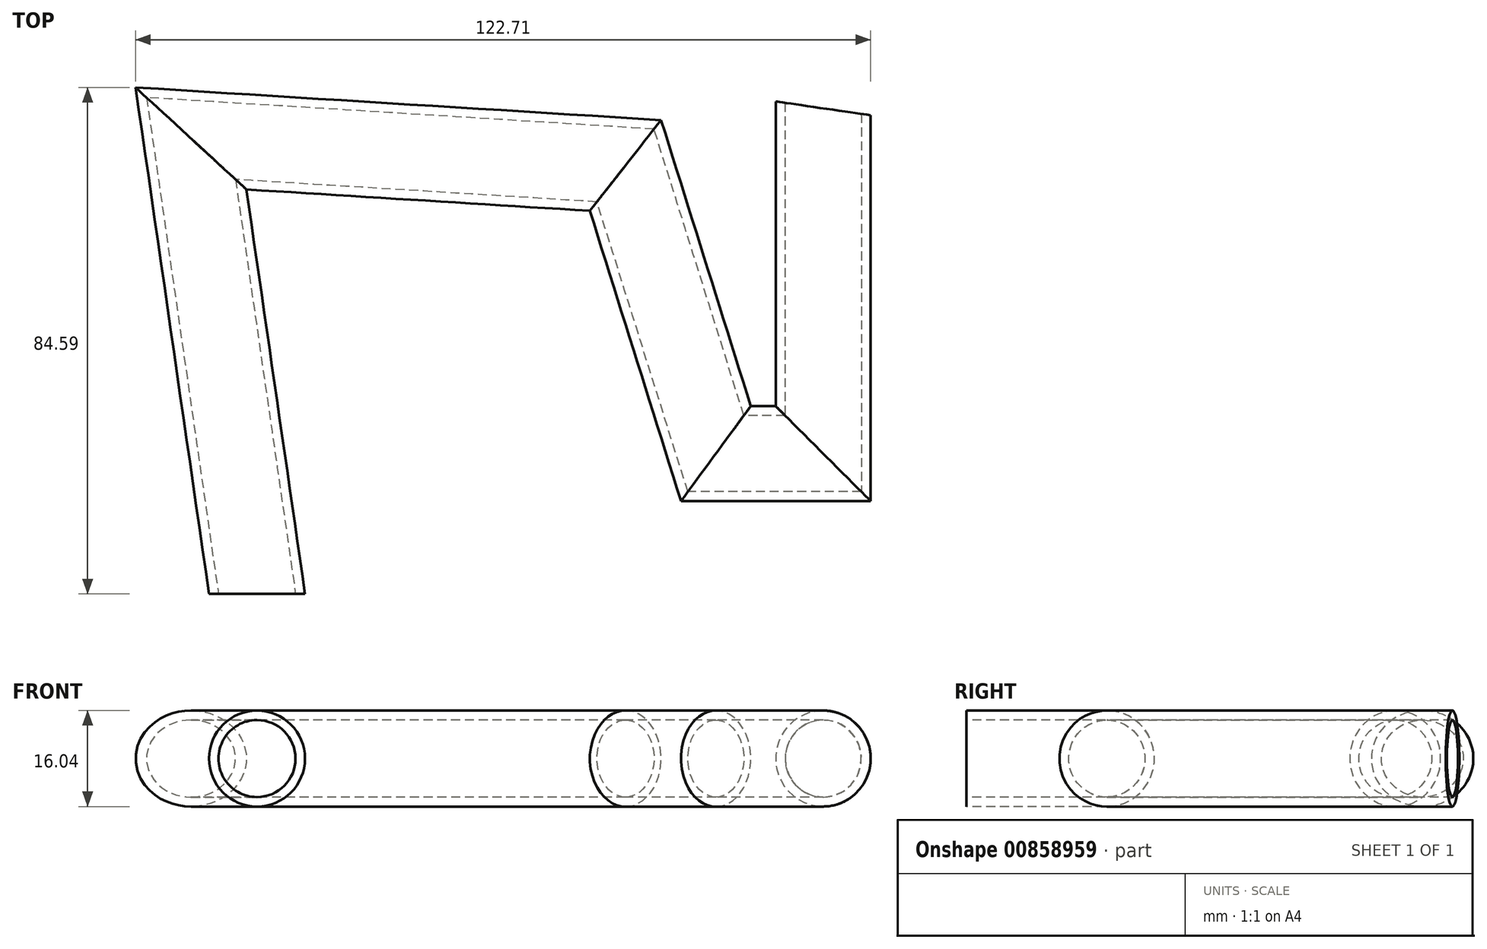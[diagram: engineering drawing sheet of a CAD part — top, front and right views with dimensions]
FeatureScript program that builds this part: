
annotation { "Feature Type Name" : "Feature", "Feature Type Description" : "" }
export const myFeature = defineFeature(function(context is Context, id is Id, definition is map)
    precondition{}
    {
        {
            var Q0;
            Q0=qCreatedBy(makeId("Top.planeOp"),FACE);
            var sketch = newSketch(context, id + "F0", { "sketchPlane" : qUnion([Q0])});
            skLineSegment(sketch, "E0", {"start": v(-37.35, -58.1) * mm, "end": v(-48, 15.52) * mm});
            skLineSegment(sketch, "E1", {"start": v(-48, 15.52) * mm, "end": v(20.13, 11.29) * mm});
            skLineSegment(sketch, "E2", {"start": v(20.13, 11.29) * mm, "end": v(35.25, -36.96) * mm});
            skLineSegment(sketch, "E3", {"start": v(35.25, -36.96) * mm, "end": v(57.14, -36.96) * mm});
            skLineSegment(sketch, "E4", {"start": v(57.14, -36.96) * mm, "end": v(57.14, 22.68) * mm});
            skSolve(sketch);
        }
        {
            var Q0;
            Q0=qCreatedBy(makeId("Front.planeOp"),FACE);
            var sketch = newSketch(context, id + "F1", { "sketchPlane" : qUnion([Q0])});
            skCircle(sketch, "E5", {"center": v(-48.07, 0) * mm, "radius": 8.02 * mm});
            skCircle(sketch, "E6", {"center": v(-48.07, 0) * mm, "radius": 6.43 * mm});
            skSolve(sketch);
        }
        {
            var Q0;
            Q0=makeQuery(id+"F1.imprint","IMPRINT",FACE,{"disambiguationData":[TD([[makeQuery(id+"F1.imprint","IMPRINT",EDGE,{"derivedFrom":sQuery(id+"F1.wireOp",EDGE,"E5")}),1.0]])]});
            var Q1;
            Q1=sQuery(id+"F0.wireOp",EDGE,"E0");
            var Q2;
            Q2=sQuery(id+"F0.wireOp",EDGE,"E1");
            var Q3;
            Q3=sQuery(id+"F0.wireOp",EDGE,"E2");
            var Q4;
            Q4=sQuery(id+"F0.wireOp",EDGE,"E3");
            var Q5;
            Q5=sQuery(id+"F0.wireOp",EDGE,"E4");
            sweep(context, id + "F2", {"profiles" : qUnion([Q0]), "path" : qUnion([Q1, Q2, Q3, Q4, Q5])});
        }
    });
